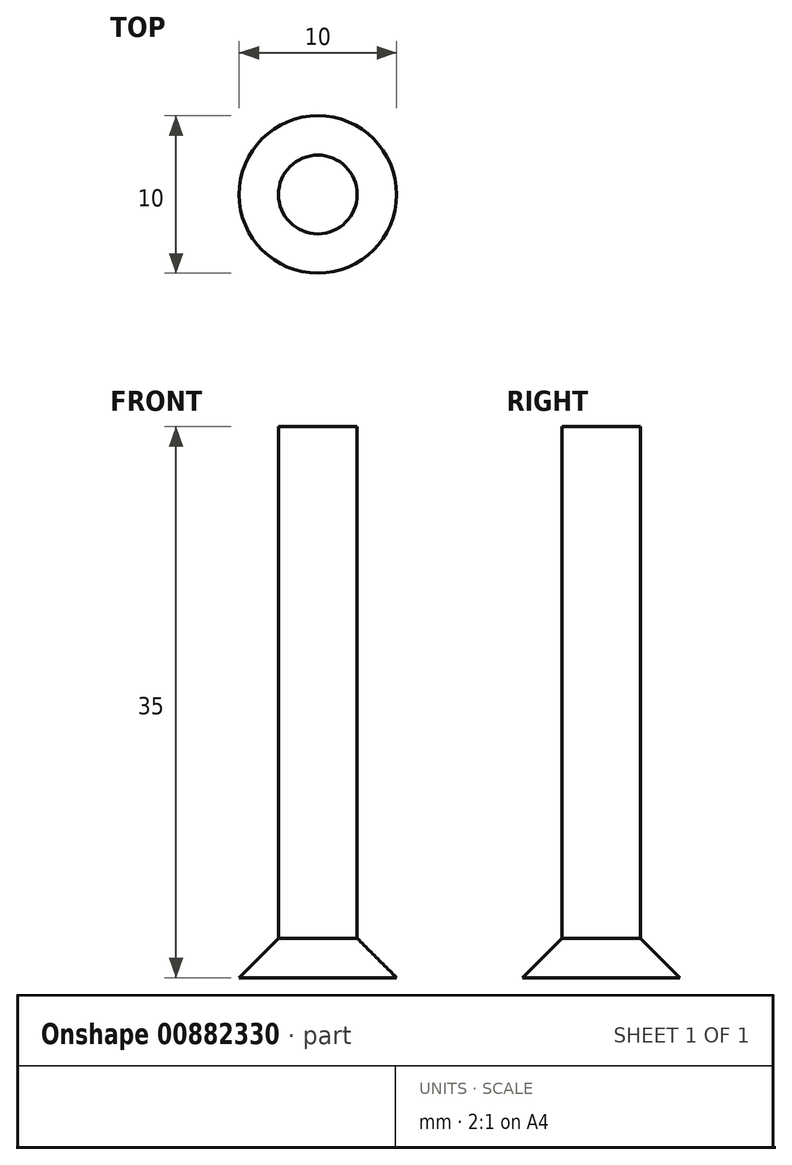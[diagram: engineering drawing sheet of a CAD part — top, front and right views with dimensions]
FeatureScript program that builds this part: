
annotation { "Feature Type Name" : "Feature", "Feature Type Description" : "" }
export const myFeature = defineFeature(function(context is Context, id is Id, definition is map)
    precondition{}
    {
        {
            var Q0;
            Q0=qCreatedBy(makeId("Top.planeOp"),FACE);
            var sketch = newSketch(context, id + "F0", { "sketchPlane" : qUnion([Q0])});
            skCircle(sketch, "E0", {"center": v(0, 0) * mm, "radius": 5 * mm});
            skPoint(sketch, "E1", {"position": v(5, 0) * mm});
            skSolve(sketch);
        }
        {
            var Q0;
            Q0 = qSketchRegion(id + "F0", true);
            extrude(context, id + "F1", {"entities" : qUnion([Q0]), "depth" : 2.5 * mm, "offsetDistance" : 25 * mm});
        }
        {
            var Q0;
            Q0=makeQuery(id+"F1.opExtrude","CAP_EDGE",EDGE,{"disambiguationData":[OSD([sQuery(id+"F0.wireOp",EDGE,"E0")])],"isStart":false});
            chamfer(context, id + "F2", {"entities" : qUnion([Q0]), "width" : 2.5 * mm, "tangentPropagation" : true});
        }
        {
            var Q0;
            Q0=makeQuery(id+"F1.opExtrude","CAP_FACE",FACE,{"disambiguationData":[OSD([sQuery(id+"F0.wireOp",EDGE,"E0")])],"isStart":false});
            extrude(context, id + "F3", {"entities" : qUnion([Q0]), "operationType" : NewBodyOperationType.ADD, "depth" : 32.5 * mm, "offsetDistance" : 25 * mm});
        }
    });
